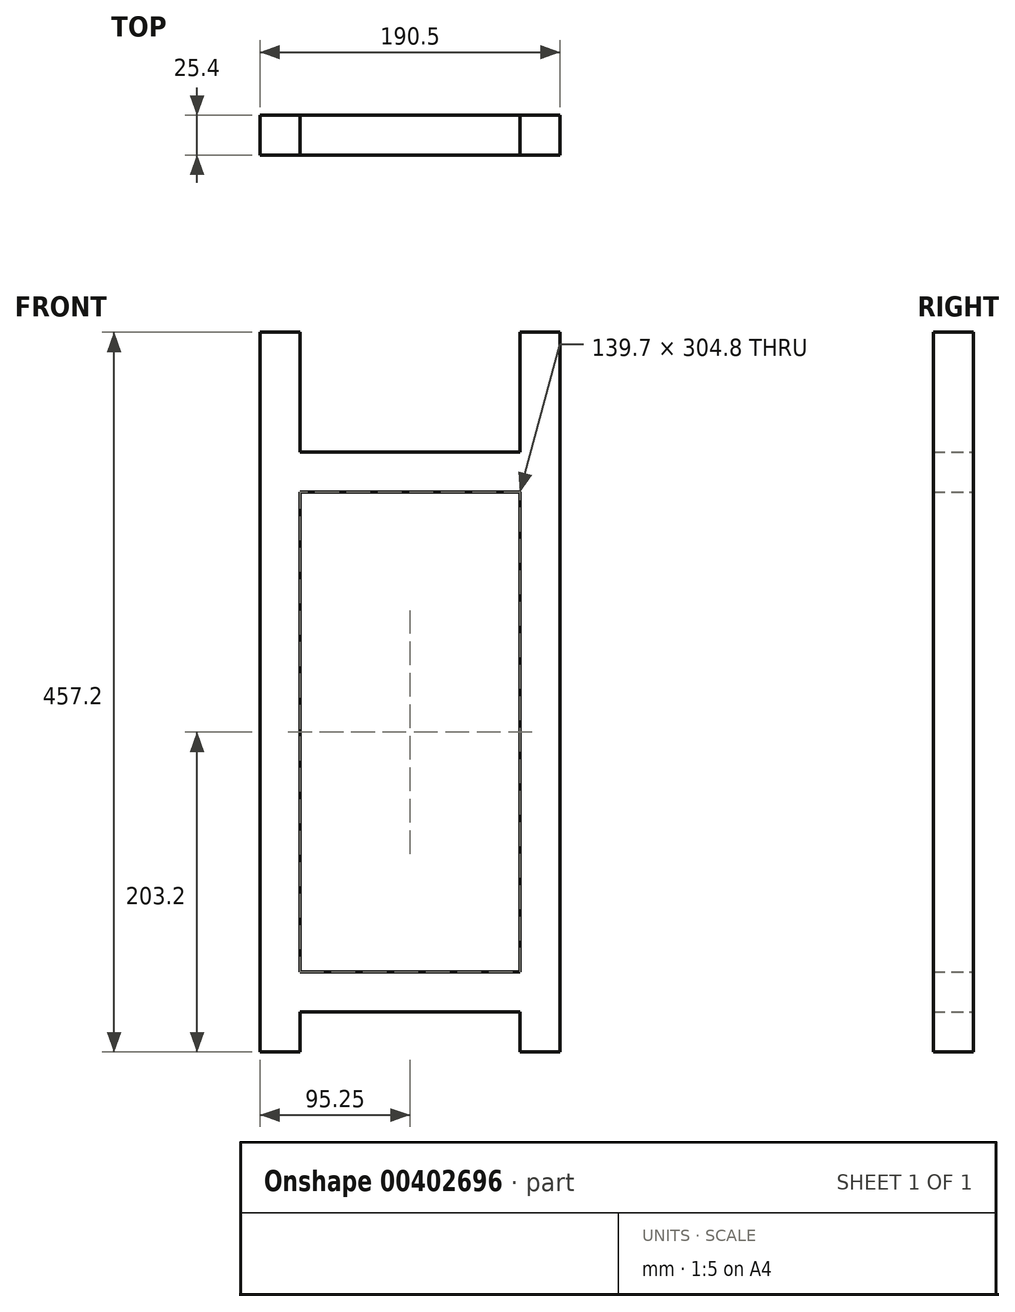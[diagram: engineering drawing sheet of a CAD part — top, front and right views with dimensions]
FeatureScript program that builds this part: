
annotation { "Feature Type Name" : "Feature", "Feature Type Description" : "" }
export const myFeature = defineFeature(function(context is Context, id is Id, definition is map)
    precondition{}
    {
        {
            var Q0;
            Q0=qCreatedBy(makeId("Front.planeOp"),FACE);
            var sketch = newSketch(context, id + "F0", { "sketchPlane" : qUnion([Q0])});
            skLineSegment(sketch, "E0.bottom", {"start": v(0, 0) * mm, "end": v(25.4, 0) * mm});
            skLineSegment(sketch, "E0.top", {"start": v(0, 457.2) * mm, "end": v(25.4, 457.2) * mm});
            skLineSegment(sketch, "E0.left", {"start": v(0, 0) * mm, "end": v(0, 457.2) * mm});
            skLineSegment(sketch, "E0.right", {"start": v(25.4, 0) * mm, "end": v(25.4, 457.2) * mm});
            skLineSegment(sketch, "E1.bottom", {"start": v(25.4, 50.8) * mm, "end": v(165.1, 50.8) * mm});
            skLineSegment(sketch, "E1.top", {"start": v(25.4, 25.4) * mm, "end": v(165.1, 25.4) * mm});
            skLineSegment(sketch, "E1.left", {"start": v(25.4, 50.8) * mm, "end": v(25.4, 25.4) * mm});
            skLineSegment(sketch, "E1.right", {"start": v(165.1, 50.8) * mm, "end": v(165.1, 25.4) * mm});
            skLineSegment(sketch, "E2.bottom", {"start": v(165.1, 457.2) * mm, "end": v(190.5, 457.2) * mm});
            skLineSegment(sketch, "E2.top", {"start": v(165.1, 0) * mm, "end": v(190.5, 0) * mm});
            skLineSegment(sketch, "E2.left", {"start": v(165.1, 457.2) * mm, "end": v(165.1, 0) * mm});
            skLineSegment(sketch, "E2.right", {"start": v(190.5, 457.2) * mm, "end": v(190.5, 0) * mm});
            skLineSegment(sketch, "E3.bottom", {"start": v(25.4, 381) * mm, "end": v(165.1, 381) * mm});
            skLineSegment(sketch, "E3.top", {"start": v(25.4, 355.6) * mm, "end": v(165.1, 355.6) * mm});
            skLineSegment(sketch, "E3.left", {"start": v(25.4, 381) * mm, "end": v(25.4, 355.6) * mm});
            skLineSegment(sketch, "E3.right", {"start": v(165.1, 381) * mm, "end": v(165.1, 355.6) * mm});
            skSolve(sketch);
        }
        {
            var Q0;
            {var subQ1=sQuery(id+"F0.wireOp",EDGE,"E0.bottom");Q0=makeQuery(id+"F0.imprint","IMPRINT",FACE,{"disambiguationData":[TD([[makeQuery(id+"F0.imprint","IMPRINT",EDGE,{"derivedFrom":subQ1}),1.0]])]});}
            var Q1;
            {var subQ3=sQuery(id+"F0.wireOp",EDGE,"E2.bottom");Q1=makeQuery(id+"F0.imprint","IMPRINT",FACE,{"disambiguationData":[TD([[makeQuery(id+"F0.imprint","IMPRINT",EDGE,{"derivedFrom":subQ3}),-1.0]])]});}
            var Q2;
            Q2=makeQuery(id+"F0.imprint","IMPRINT",FACE,{"disambiguationData":[TD([[makeQuery(id+"F0.imprint","IMPRINT",EDGE,{"derivedFrom":sQuery(id+"F0.wireOp",EDGE,"E3.bottom")}),-1.0]])]});
            var Q3;
            {var subQ0=sQuery(id+"F0.wireOp",EDGE,"E1.bottom");Q3=makeQuery(id+"F0.imprint","IMPRINT",FACE,{"disambiguationData":[TD([[makeQuery(id+"F0.imprint","IMPRINT",EDGE,{"derivedFrom":subQ0}),-1.0]])]});}
            extrude(context, id + "F1", {"entities" : qUnion([Q0, Q1, Q2, Q3]), "depth" : 25.4 * mm});
        }
    });
